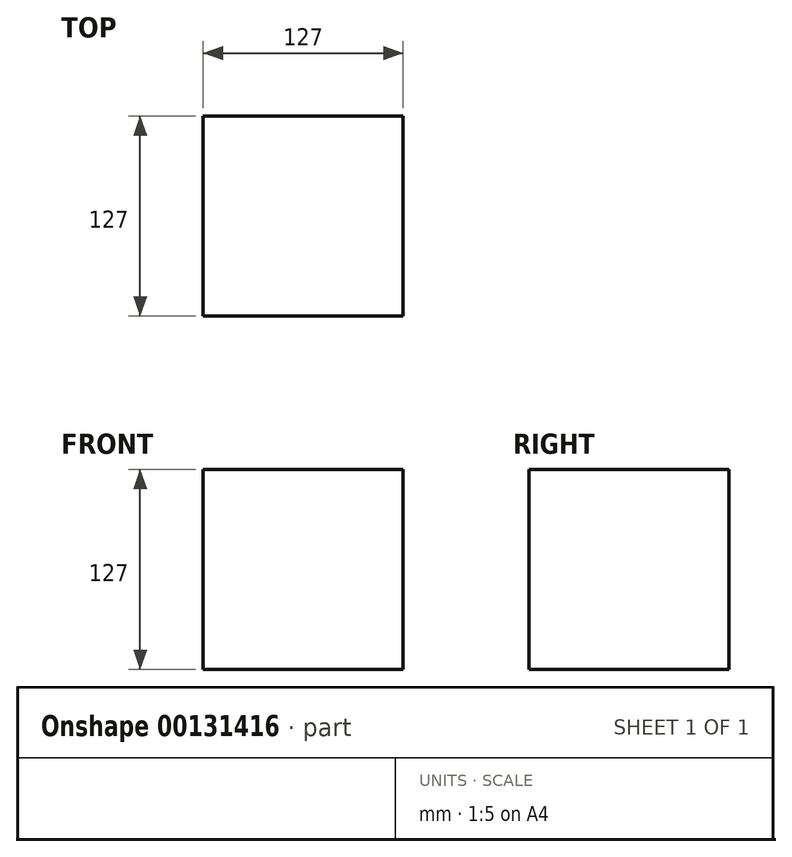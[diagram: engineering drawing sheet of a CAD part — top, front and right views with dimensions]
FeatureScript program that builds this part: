
annotation { "Feature Type Name" : "Feature", "Feature Type Description" : "" }
export const myFeature = defineFeature(function(context is Context, id is Id, definition is map)
    precondition{}
    {
        {
            var Q0;
            Q0=qCreatedBy(makeId("Front.planeOp"),FACE);
            var sketch = newSketch(context, id + "F0", { "sketchPlane" : qUnion([Q0])});
            skLineSegment(sketch, "E0.bottom", {"start": v(63.5, 63.5) * mm, "end": v(-63.5, 63.5) * mm});
            skLineSegment(sketch, "E0.top", {"start": v(63.5, -63.5) * mm, "end": v(-63.5, -63.5) * mm});
            skLineSegment(sketch, "E0.left", {"start": v(63.5, 63.5) * mm, "end": v(63.5, -63.5) * mm});
            skLineSegment(sketch, "E0.right", {"start": v(-63.5, 63.5) * mm, "end": v(-63.5, -63.5) * mm});
            skPoint(sketch, "E0.middle", {"position": v(0, 0) * mm});
            skSolve(sketch);
        }
        {
            var Q0;
            Q0=makeQuery(id+"F0.imprint","IMPRINT",FACE,{"disambiguationData":[TD([[makeQuery(id+"F0.imprint","IMPRINT",EDGE,{"derivedFrom":sQuery(id+"F0.wireOp",EDGE,"E0.bottom")}),1.0]])]});
            extrude(context, id + "F1", {"entities" : qUnion([Q0]), "endBound" : BoundingType.SYMMETRIC, "depth" : 127 * mm});
        }
    });
